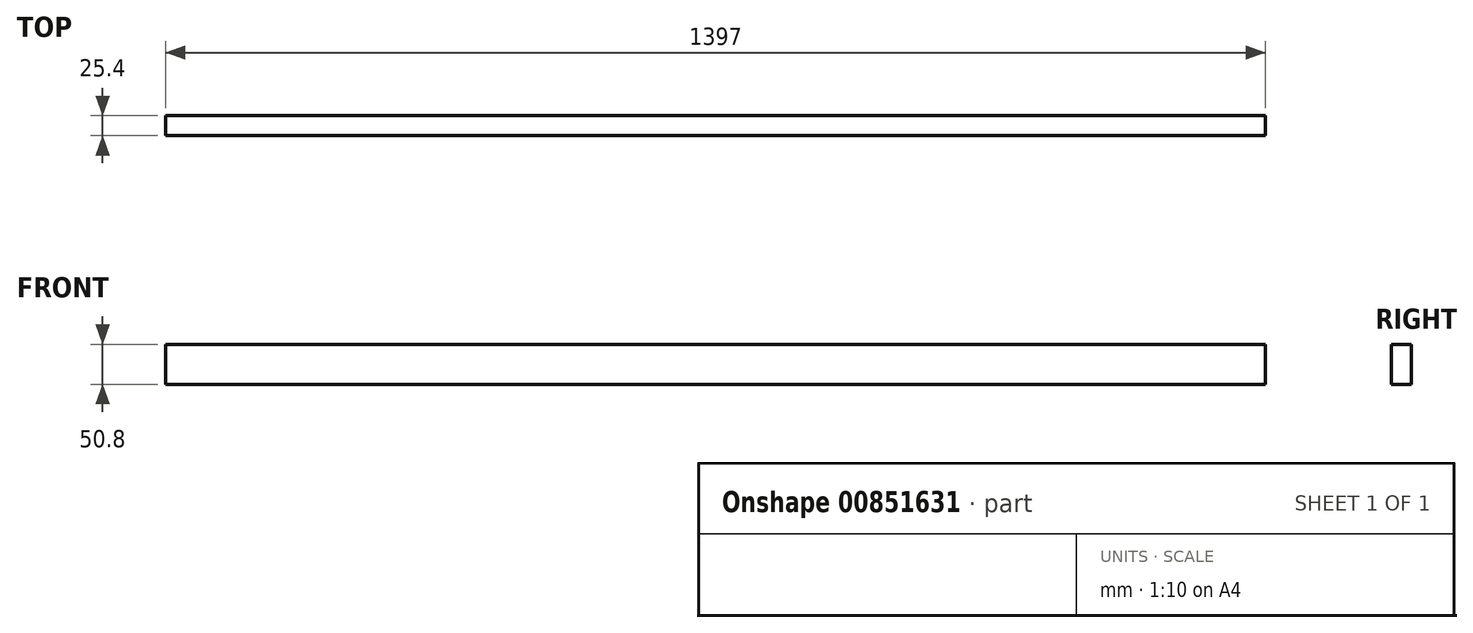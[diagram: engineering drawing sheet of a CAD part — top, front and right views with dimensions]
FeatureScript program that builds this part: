
annotation { "Feature Type Name" : "Feature", "Feature Type Description" : "" }
export const myFeature = defineFeature(function(context is Context, id is Id, definition is map)
    precondition{}
    {
        {
            var Q0;
            Q0=qCreatedBy(makeId("Front.planeOp"),FACE);
            var sketch = newSketch(context, id + "F0", { "sketchPlane" : qUnion([Q0])});
            skLineSegment(sketch, "E0", {"start": v(651.86, -56.63) * mm, "end": v(-745.14, -56.63) * mm});
            skLineSegment(sketch, "E1", {"start": v(-745.14, -56.63) * mm, "end": v(-745.14, -107.43) * mm});
            skLineSegment(sketch, "E2", {"start": v(651.86, -56.63) * mm, "end": v(651.86, -107.43) * mm});
            skLineSegment(sketch, "E3", {"start": v(651.86, -107.43) * mm, "end": v(-745.14, -107.43) * mm});
            skSolve(sketch);
        }
        {
            var Q0;
            Q0 = qSketchRegion(id + "F0", true);
            extrude(context, id + "F1", {"entities" : qUnion([Q0]), "depth" : 25.4 * mm, "offsetDistance" : 25.4 * mm});
        }
    });
